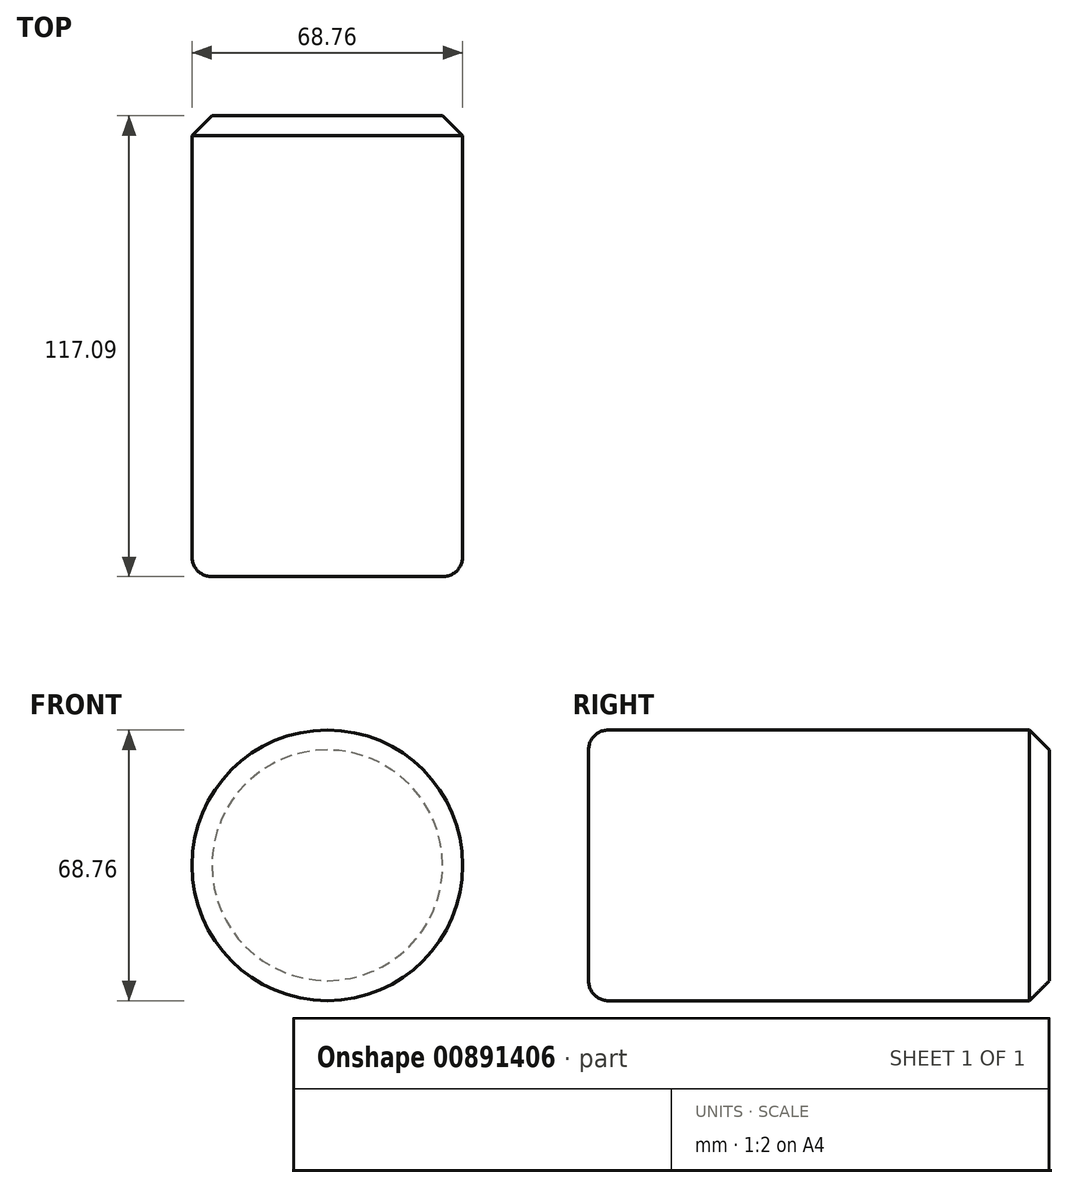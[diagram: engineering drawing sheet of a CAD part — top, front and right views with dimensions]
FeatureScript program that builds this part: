
annotation { "Feature Type Name" : "Feature", "Feature Type Description" : "" }
export const myFeature = defineFeature(function(context is Context, id is Id, definition is map)
    precondition{}
    {
        {
            var Q0;
            Q0=qCreatedBy(makeId("Front.planeOp"),FACE);
            var sketch = newSketch(context, id + "F0", { "sketchPlane" : qUnion([Q0])});
            skCircle(sketch, "E0", {"center": v(0, 0) * mm, "radius": 34.38 * mm});
            skSolve(sketch);
        }
        {
            var Q0;
            Q0=makeQuery(id+"F0.imprint","IMPRINT",FACE,{"disambiguationData":[TD([[makeQuery(id+"F0.imprint","IMPRINT",EDGE,{"derivedFrom":sQuery(id+"F0.wireOp",EDGE,"E0")}),1.0]])]});
            var Q1;
            Q1=sQuery(id+"F0.wireOp",EDGE,"E0");
            extrude(context, id + "F1", {"entities" : qUnion([Q0]), "surfaceEntities" : qUnion([Q1]), "depth" : 117.1 * mm, "offsetDistance" : 25.4 * mm});
        }
        {
            var Q0;
            Q0=makeQuery(id+"F1.opExtrude","CAP_EDGE",EDGE,{"disambiguationData":[OSD([sQuery(id+"F0.wireOp",EDGE,"E0")])],"isStart":true});
            chamfer(context, id + "F2", {"entities" : qUnion([Q0]), "width" : 5.08 * mm, "tangentPropagation" : true});
        }
        {
            var Q0;
            Q0=makeQuery(id+"F1.opExtrude","CAP_EDGE",EDGE,{"disambiguationData":[OSD([sQuery(id+"F0.wireOp",EDGE,"E0")])],"isStart":false});
            fillet(context, id + "F3", {"entities" : qUnion([Q0]), "radius" : 5 * mm, "tangentPropagation" : true, "allowEdgeOverflow" : false});
        }
    });
